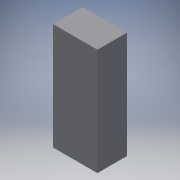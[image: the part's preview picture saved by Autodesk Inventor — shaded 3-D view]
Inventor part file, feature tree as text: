
AUTODESK INVENTOR PART (.ipt)
format: ipt  version: 2018 (Build 220112000, 112)  size: 88,576 bytes
history: native  units: in
note: dims shown in document units (in); Inventor stores cm internally (conversion verified against a paired STEP export)
features: extrude x1, sketch x1
ambient origin geometry x8: Origin, YZ Plane, XZ Plane, XY Plane, X Axis, Y Axis, Z Axis, Center Point
bodies: Solid1 (feature_tree)
feature tree (2):
  extrude  "Extrusion1"  Depth=36.0in
  sketch  "Sketch1"  dims[d0=12.0in d1=36.0in d2=10.0in d3=0.0in]
